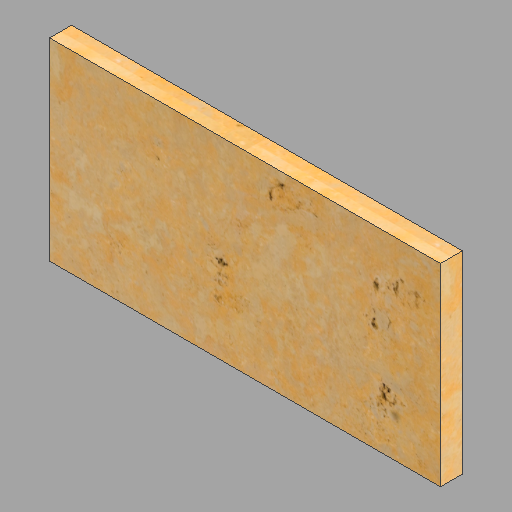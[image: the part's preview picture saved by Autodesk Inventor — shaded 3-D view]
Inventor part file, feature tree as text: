
AUTODESK INVENTOR PART (.ipt)
format: ipt  version: 2023 (Build 270158030, 158C)  size: 323,072 bytes
history: native  units: in
note: dims shown in document units (in); Inventor stores cm internally (conversion verified against a paired STEP export)
features: extrude x1, sketch x1
ambient origin geometry x8: Origin, YZ Plane, XZ Plane, XY Plane, X Axis, Y Axis, Z Axis, Center Point
bodies: Solid1 (feature_tree)
feature tree (2):
  extrude  "Extrusion1"  Depth=2.0in
  sketch  "Sketch1"  dims[d0=35.625in d1=2.0in d2=17.625in d3=0.0in]
